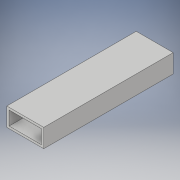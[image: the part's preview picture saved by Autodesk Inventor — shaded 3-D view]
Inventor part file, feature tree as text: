
AUTODESK INVENTOR PART (.ipt)
format: ipt  version: 2017 (Build 210142000, 142)  size: 97,792 bytes
history: native  units: in
note: dims shown in document units (in); Inventor stores cm internally (conversion verified against a paired STEP export)
features: extrude x1, sketch x1
ambient origin geometry x8: Origin, YZ Plane, XZ Plane, XY Plane, X Axis, Y Axis, Z Axis, Center Point
bodies: Solid1 (feature_tree)
feature tree (2):
  extrude  "Extrusion1"  Depth=1.0in
  sketch  "Sketch1"  dims[d0=2.0in d1=1.0in d2=1.75in d3=0.75in d4=0.125in d5=0.125in d6=7.0in d7=0.0in]
